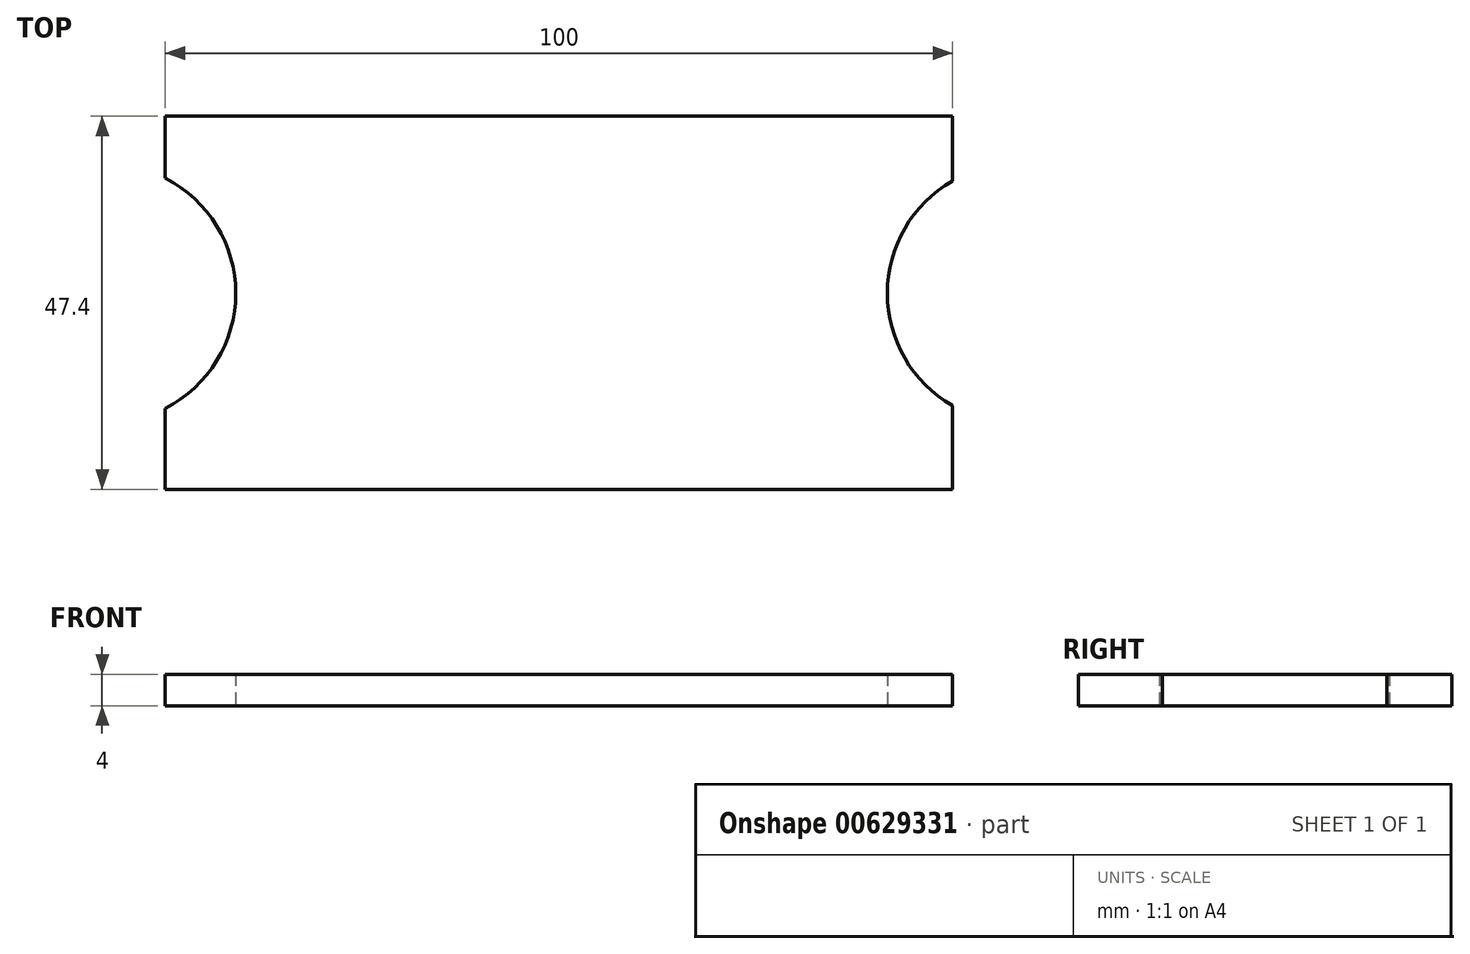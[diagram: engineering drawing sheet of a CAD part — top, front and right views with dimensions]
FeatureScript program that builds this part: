
annotation { "Feature Type Name" : "Feature", "Feature Type Description" : "" }
export const myFeature = defineFeature(function(context is Context, id is Id, definition is map)
    precondition{}
    {
        {
            var Q0;
            Q0=qCreatedBy(makeId("Top.planeOp"),FACE);
            var sketch = newSketch(context, id + "F0", { "sketchPlane" : qUnion([Q0])});
            skLineSegment(sketch, "E0.bottom", {"start": v(50, -23.7) * mm, "end": v(-50, -23.7) * mm});
            skLineSegment(sketch, "E0.top", {"start": v(50, 23.7) * mm, "end": v(-50, 23.7) * mm});
            skLineSegment(sketch, "E0.left", {"start": v(50, -23.7) * mm, "end": v(50, -13.06) * mm});
            skLineSegment(sketch, "E0.right", {"start": v(-50, -23.7) * mm, "end": v(-50, -13.41) * mm});
            skPoint(sketch, "E0.middle", {"position": v(0, 0) * mm});
            skArc(sketch, "E1", {"start": v(-50, -13.41) * mm, "mid": v(-41.05, 1.2) * mm, "end": v(-50, 15.81) * mm});
            skArc(sketch, "E2", {"start": v(50, 15.46) * mm, "mid": v(41.7, 1.2) * mm, "end": v(50, -13.06) * mm});
            skLineSegment(sketch, "E3.trimOffspring", {"start": v(-50, 15.81) * mm, "end": v(-50, 23.7) * mm});
            skLineSegment(sketch, "E4.trimOffspring", {"start": v(50, 15.46) * mm, "end": v(50, 23.7) * mm});
            skSolve(sketch);
        }
        {
            var Q0;
            {var subQ4=sQuery(id+"F0.wireOp",EDGE,"E0.bottom");Q0=makeQuery(id+"F0.imprint","IMPRINT",FACE,{"disambiguationData":[TD([[makeQuery(id+"F0.imprint","IMPRINT",EDGE,{"derivedFrom":subQ4}),-1.0]])]});}
            extrude(context, id + "F1", {"entities" : qUnion([Q0]), "depth" : 2 * mm, "offsetDistance" : 25 * mm});
        }
        {
            var Q0;
            Q0=makeQuery(id+"F1.opExtrude","CAP_FACE",FACE,{"disambiguationData":[OSD([sQuery(id+"F0.wireOp",EDGE,"E0.bottom"),sQuery(id+"F0.wireOp",EDGE,"E0.top"),sQuery(id+"F0.wireOp",EDGE,"E0.left"),sQuery(id+"F0.wireOp",EDGE,"E0.right"),sQuery(id+"F0.wireOp",EDGE,"E1"),sQuery(id+"F0.wireOp",EDGE,"E2")])],"isStart":false});
            extrude(context, id + "F2", {"entities" : qUnion([Q0]), "operationType" : NewBodyOperationType.ADD, "depth" : 2 * mm, "offsetDistance" : 25 * mm});
        }
    });
